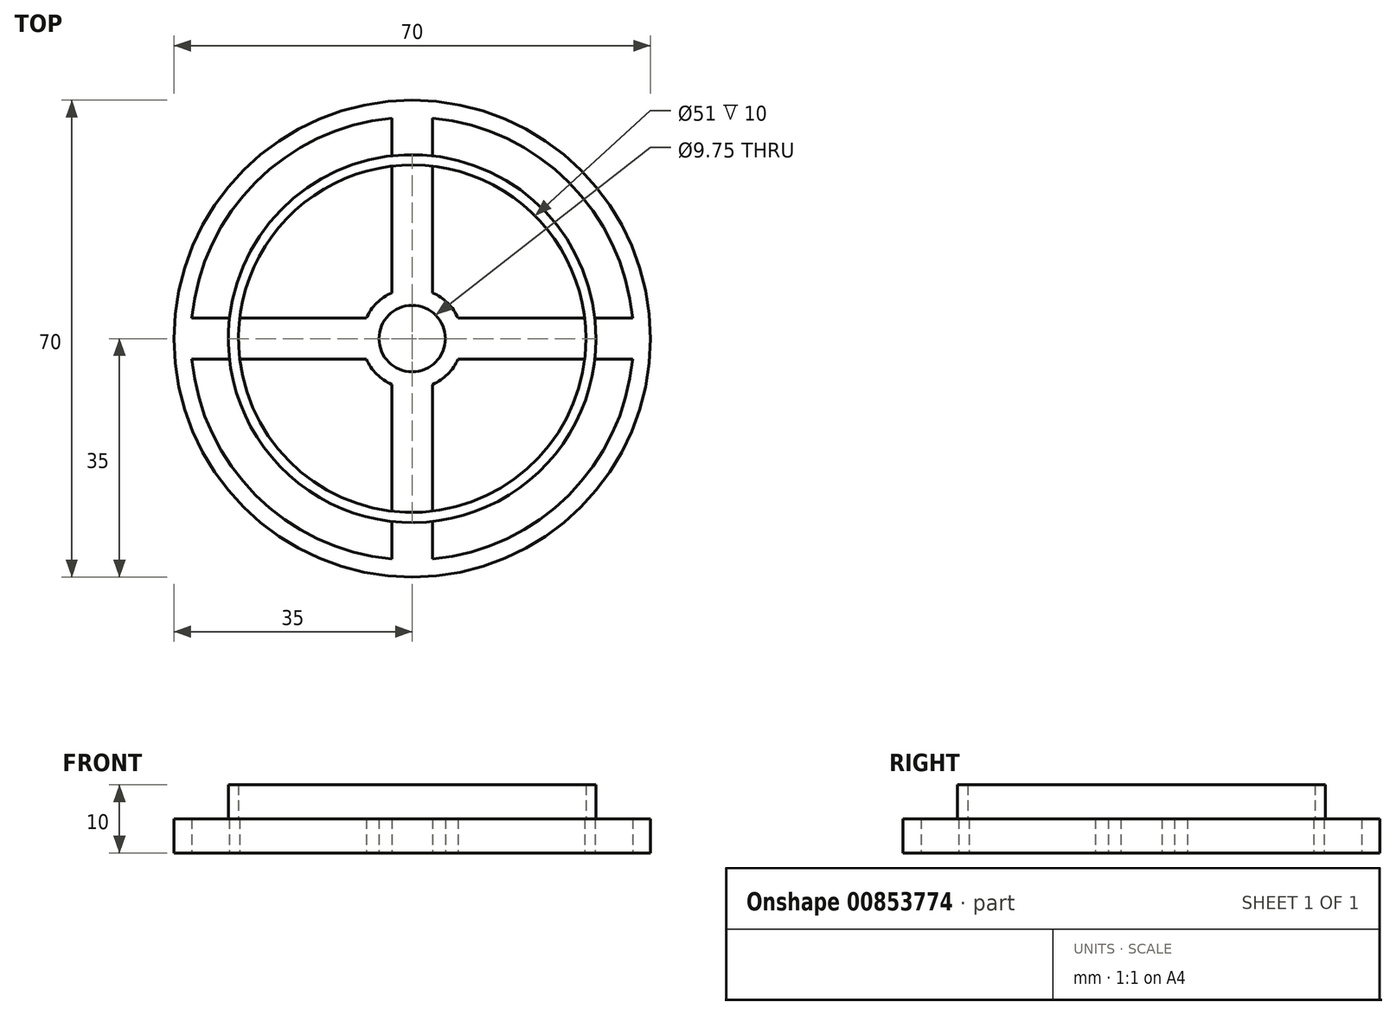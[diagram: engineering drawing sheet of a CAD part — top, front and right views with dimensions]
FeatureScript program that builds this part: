
annotation { "Feature Type Name" : "Feature", "Feature Type Description" : "" }
export const myFeature = defineFeature(function(context is Context, id is Id, definition is map)
    precondition{}
    {
        {
            var Q0;
            Q0=qCreatedBy(makeId("Top.planeOp"),FACE);
            var sketch = newSketch(context, id + "F0", { "sketchPlane" : qUnion([Q0])});
            skCircle(sketch, "E0", {"center": v(0, 0) * mm, "radius": 4.88 * mm});
            skCircle(sketch, "E1", {"center": v(0, 0) * mm, "radius": 35 * mm});
            skCircle(sketch, "E2", {"center": v(0, 0) * mm, "radius": 24 * mm});
            skCircle(sketch, "E3", {"center": v(0, 0) * mm, "radius": 7.38 * mm});
            skLineSegment(sketch, "E4", {"start": v(0, 7.38) * mm, "end": v(0, 0) * mm});
            skLineSegment(sketch, "E5", {"start": v(0, 0) * mm, "end": v(-7.38, 0) * mm});
            skLineSegment(sketch, "E6", {"start": v(0, 0) * mm, "end": v(7.38, 0) * mm});
            skLineSegment(sketch, "E7", {"start": v(0, 0) * mm, "end": v(0, -7.38) * mm});
            skLineSegment(sketch, "E8", {"start": v(3, -23.81) * mm, "end": v(3, -6.74) * mm});
            skLineSegment(sketch, "E9", {"start": v(-3, -23.81) * mm, "end": v(-3, -6.74) * mm});
            skLineSegment(sketch, "E10", {"start": v(-23.81, -3) * mm, "end": v(-6.74, -3) * mm});
            skLineSegment(sketch, "E11", {"start": v(-3, 23.81) * mm, "end": v(-3, 6.74) * mm});
            skLineSegment(sketch, "E12", {"start": v(3, 23.81) * mm, "end": v(3, 6.74) * mm});
            skLineSegment(sketch, "E13", {"start": v(23.81, 3) * mm, "end": v(6.74, 3) * mm});
            skLineSegment(sketch, "E14", {"start": v(23.81, -3) * mm, "end": v(6.74, -3) * mm});
            skLineSegment(sketch, "E15", {"start": v(-23.81, 3) * mm, "end": v(-6.74, 3) * mm});
            skPoint(sketch, "E16.orphan", {"position": v(0, 24) * mm});
            skCircle(sketch, "E17", {"center": v(0, 0) * mm, "radius": 32.5 * mm});
            skLineSegment(sketch, "E18", {"start": v(-3, 23.81) * mm, "end": v(-3, 32.36) * mm});
            skLineSegment(sketch, "E19", {"start": v(3, 23.81) * mm, "end": v(3, 32.36) * mm});
            skLineSegment(sketch, "E20", {"start": v(23.81, 3) * mm, "end": v(32.36, 3) * mm});
            skLineSegment(sketch, "E21", {"start": v(23.81, -3) * mm, "end": v(32.36, -3) * mm});
            skLineSegment(sketch, "E22", {"start": v(3, -23.81) * mm, "end": v(3, -32.36) * mm});
            skLineSegment(sketch, "E23", {"start": v(-3, -23.81) * mm, "end": v(-3, -32.36) * mm});
            skLineSegment(sketch, "E24", {"start": v(-23.81, 3) * mm, "end": v(-32.36, 3) * mm});
            skLineSegment(sketch, "E25", {"start": v(-23.81, -3) * mm, "end": v(-32.36, -3) * mm});
            skCircle(sketch, "E26", {"center": v(0, 0) * mm, "radius": 25.5 * mm});
            skCircle(sketch, "E27", {"center": v(0, 0) * mm, "radius": 27 * mm});
            skSolve(sketch);
        }
        {
            var Q0;
            Q0 = qSketchRegion(id + "F0", true);
            var Q1;
            {var subQ0=sQuery(id+"F0.wireOp",EDGE,"E10");Q1=makeQuery(id+"F0.imprint","IMPRINT",FACE,{"disambiguationData":[TD([[makeQuery(id+"F0.imprint","IMPRINT",EDGE,{"derivedFrom":subQ0}),1.0]])]});}
            var Q2;
            {var subQ5=sQuery(id+"F0.wireOp",EDGE,"E0");var subQ7=sQuery(id+"F0.wireOp",EDGE,"E4");var subQ9=makeQuery(id+"F0.imprint","INTERSECT",VERTEX,{"derivedFrom":[subQ5,subQ7]});Q2=makeQuery(id+"F0.imprint","IMPRINT",FACE,{"disambiguationData":[TD([[makeQuery(id+"F0.imprint","IMPRINT",EDGE,{"disambiguationData":[TD([[subQ9,-1.0]])],"derivedFrom":subQ5}),-1.0]])]});}
            var Q3;
            {var subQ4=sQuery(id+"F0.wireOp",EDGE,"E0");var subQ7=sQuery(id+"F0.wireOp",EDGE,"E5");var subQ9=makeQuery(id+"F0.imprint","INTERSECT",VERTEX,{"derivedFrom":[subQ4,subQ7]});Q3=makeQuery(id+"F0.imprint","IMPRINT",FACE,{"disambiguationData":[TD([[makeQuery(id+"F0.imprint","IMPRINT",EDGE,{"disambiguationData":[TD([[subQ9,-1.0]])],"derivedFrom":subQ4}),-1.0]])]});}
            var Q4;
            {var subQ0=sQuery(id+"F0.wireOp",EDGE,"E6");var subQ7=sQuery(id+"F0.wireOp",EDGE,"E0");var subQ8=makeQuery(id+"F0.imprint","INTERSECT",VERTEX,{"derivedFrom":[subQ7,subQ0]});Q4=makeQuery(id+"F0.imprint","IMPRINT",FACE,{"disambiguationData":[TD([[makeQuery(id+"F0.imprint","IMPRINT",EDGE,{"disambiguationData":[TD([[subQ8,1.0]])],"derivedFrom":subQ7}),-1.0]])]});}
            var Q5;
            {var subQ3=sQuery(id+"F0.wireOp",EDGE,"E4");var subQ5=sQuery(id+"F0.wireOp",EDGE,"E0");var subQ6=makeQuery(id+"F0.imprint","INTERSECT",VERTEX,{"derivedFrom":[subQ5,subQ3]});Q5=makeQuery(id+"F0.imprint","IMPRINT",FACE,{"disambiguationData":[TD([[makeQuery(id+"F0.imprint","IMPRINT",EDGE,{"disambiguationData":[TD([[subQ6,1.0]])],"derivedFrom":subQ5}),-1.0]])]});}
            var Q6;
            {var subQ3=sQuery(id+"F0.wireOp",EDGE,"E11");Q6=makeQuery(id+"F0.imprint","IMPRINT",FACE,{"disambiguationData":[TD([[makeQuery(id+"F0.imprint","IMPRINT",EDGE,{"derivedFrom":subQ3}),1.0]])]});}
            var Q7;
            {var subQ3=sQuery(id+"F0.wireOp",EDGE,"E13");Q7=makeQuery(id+"F0.imprint","IMPRINT",FACE,{"disambiguationData":[TD([[makeQuery(id+"F0.imprint","IMPRINT",EDGE,{"derivedFrom":subQ3}),1.0]])]});}
            var Q8;
            {var subQ0=sQuery(id+"F0.wireOp",EDGE,"E8");Q8=makeQuery(id+"F0.imprint","IMPRINT",FACE,{"disambiguationData":[TD([[makeQuery(id+"F0.imprint","IMPRINT",EDGE,{"derivedFrom":subQ0}),1.0]])]});}
            var Q9;
            {var subQ0=sQuery(id+"F0.wireOp",EDGE,"E18");Q9=makeQuery(id+"F0.imprint","IMPRINT",FACE,{"disambiguationData":[TD([[makeQuery(id+"F0.imprint","IMPRINT",EDGE,{"derivedFrom":subQ0}),-1.0]])]});}
            var Q10;
            {var subQ0=sQuery(id+"F0.wireOp",EDGE,"E20");Q10=makeQuery(id+"F0.imprint","IMPRINT",FACE,{"disambiguationData":[TD([[makeQuery(id+"F0.imprint","IMPRINT",EDGE,{"derivedFrom":subQ0}),-1.0]])]});}
            var Q11;
            {var subQ2=sQuery(id+"F0.wireOp",EDGE,"E24");Q11=makeQuery(id+"F0.imprint","IMPRINT",FACE,{"disambiguationData":[TD([[makeQuery(id+"F0.imprint","IMPRINT",EDGE,{"derivedFrom":subQ2}),1.0]])]});}
            var Q12;
            {var subQ0=sQuery(id+"F0.wireOp",EDGE,"E22");Q12=makeQuery(id+"F0.imprint","IMPRINT",FACE,{"disambiguationData":[TD([[makeQuery(id+"F0.imprint","IMPRINT",EDGE,{"derivedFrom":subQ0}),-1.0]])]});}
            var Q13;
            {var subQ0=sQuery(id+"F0.wireOp",EDGE,"E26");var subQ1=sQuery(id+"F0.wireOp",EDGE,"E18");var subQ2=makeQuery(id+"F0.imprint","INTERSECT",VERTEX,{"derivedFrom":[subQ1,subQ0]});Q13=makeQuery(id+"F0.imprint","IMPRINT",FACE,{"disambiguationData":[TD([[makeQuery(id+"F0.imprint","IMPRINT",EDGE,{"disambiguationData":[TD([[subQ2,-1.0]])],"derivedFrom":subQ1}),1.0]])]});}
            var Q14;
            {var subQ0=sQuery(id+"F0.wireOp",EDGE,"E26");var subQ1=sQuery(id+"F0.wireOp",EDGE,"E19");var subQ2=makeQuery(id+"F0.imprint","INTERSECT",VERTEX,{"derivedFrom":[subQ1,subQ0]});Q14=makeQuery(id+"F0.imprint","IMPRINT",FACE,{"disambiguationData":[TD([[makeQuery(id+"F0.imprint","IMPRINT",EDGE,{"disambiguationData":[TD([[subQ2,-1.0]])],"derivedFrom":subQ1}),-1.0]])]});}
            var Q15;
            {var subQ0=sQuery(id+"F0.wireOp",EDGE,"E26");var subQ1=sQuery(id+"F0.wireOp",EDGE,"E21");var subQ2=makeQuery(id+"F0.imprint","INTERSECT",VERTEX,{"derivedFrom":[subQ1,subQ0]});Q15=makeQuery(id+"F0.imprint","IMPRINT",FACE,{"disambiguationData":[TD([[makeQuery(id+"F0.imprint","IMPRINT",EDGE,{"disambiguationData":[TD([[subQ2,-1.0]])],"derivedFrom":subQ1}),-1.0]])]});}
            var Q16;
            {var subQ0=sQuery(id+"F0.wireOp",EDGE,"E26");var subQ1=sQuery(id+"F0.wireOp",EDGE,"E23");var subQ2=makeQuery(id+"F0.imprint","INTERSECT",VERTEX,{"derivedFrom":[subQ1,subQ0]});Q16=makeQuery(id+"F0.imprint","IMPRINT",FACE,{"disambiguationData":[TD([[makeQuery(id+"F0.imprint","IMPRINT",EDGE,{"disambiguationData":[TD([[subQ2,-1.0]])],"derivedFrom":subQ1}),-1.0]])]});}
            extrude(context, id + "F1", {"entities" : qUnion([Q0, Q1, Q2, Q3, Q4, Q5, Q6, Q7, Q8, Q9, Q10, Q11, Q12, Q13, Q14, Q15, Q16]), "depth" : 5 * mm, "offsetDistance" : 25 * mm});
        }
        {
            var Q0;
            Q0=makeQuery(id+"F1.opExtrude","CAP_FACE",FACE,{"disambiguationData":[OSD([sQuery(id+"F0.wireOp",EDGE,"E0"),sQuery(id+"F0.wireOp",EDGE,"E1")])],"isStart":false});
            var sketch = newSketch(context, id + "F2", { "sketchPlane" : qUnion([Q0])});
            skCircle(sketch, "E28", {"center": v(0, 0) * mm, "radius": 27 * mm});
            skCircle(sketch, "E29", {"center": v(0, 0) * mm, "radius": 25.5 * mm});
            skSolve(sketch);
        }
        {
            var Q0;
            Q0 = qSketchRegion(id + "F2", true);
            extrude(context, id + "F3", {"entities" : qUnion([Q0]), "operationType" : NewBodyOperationType.ADD, "depth" : 5 * mm, "offsetDistance" : 25 * mm});
        }
    });
